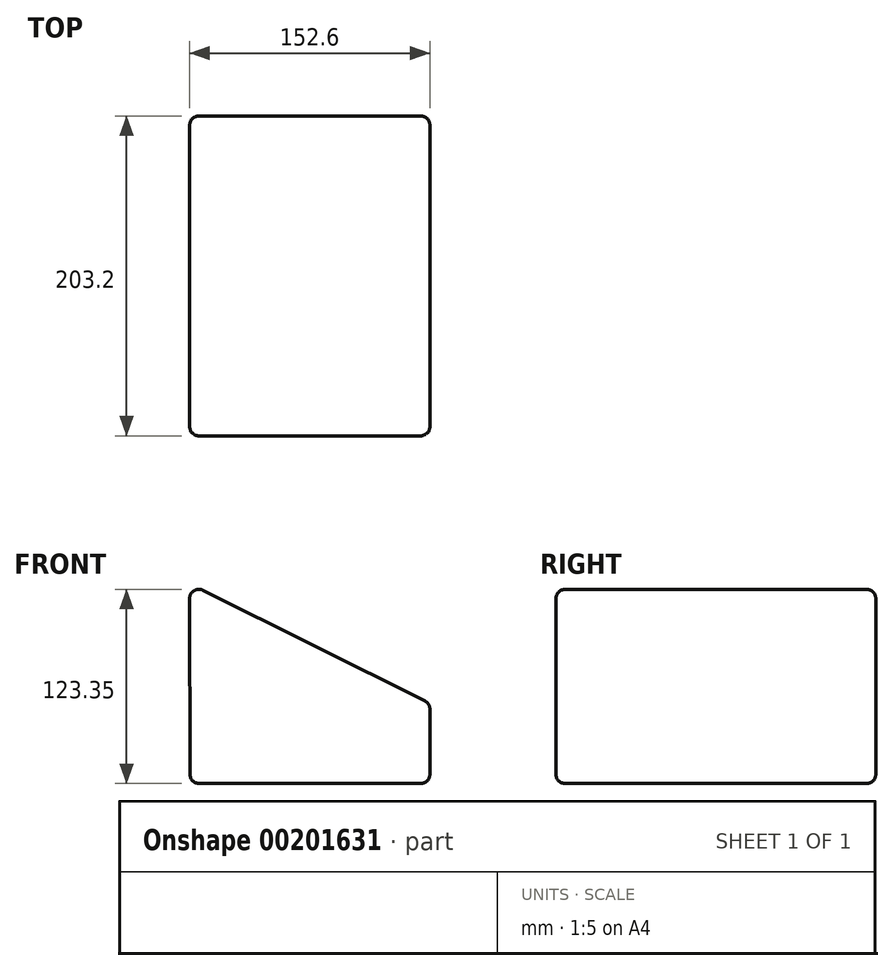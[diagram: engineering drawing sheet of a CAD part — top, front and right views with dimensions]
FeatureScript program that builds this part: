
annotation { "Feature Type Name" : "Feature", "Feature Type Description" : "" }
export const myFeature = defineFeature(function(context is Context, id is Id, definition is map)
    precondition{}
    {
        {
            var Q0;
            Q0=qCreatedBy(makeId("Front.planeOp"),FACE);
            var sketch = newSketch(context, id + "F0", { "sketchPlane" : qUnion([Q0])});
            skLineSegment(sketch, "E0", {"start": v(76.24, 0) * mm, "end": v(76.24, 50.8) * mm});
            skLineSegment(sketch, "E1", {"start": v(76.24, 50.8) * mm, "end": v(-76.38, 127) * mm});
            skLineSegment(sketch, "E2", {"start": v(-76.16, 0) * mm, "end": v(76.24, 0) * mm});
            skLineSegment(sketch, "E3", {"start": v(-76.38, 127) * mm, "end": v(-76.16, 0) * mm});
            skSolve(sketch);
        }
        {
            var Q0;
            Q0 = qSketchRegion(id + "F0", true);
            extrude(context, id + "F1", {"entities" : qUnion([Q0]), "endBound" : BoundingType.SYMMETRIC, "depth" : 203.2 * mm});
        }
        {
            var Q0;
            Q0=makeQuery(id+"F1.opExtrude","SWEPT_FACE",FACE,{"disambiguationData":[OSD([sQuery(id+"F0.wireOp",EDGE,"E1")])]});
            var Q1;
            Q1=makeQuery(id+"F1.opExtrude","SWEPT_FACE",FACE,{"disambiguationData":[OSD([sQuery(id+"F0.wireOp",EDGE,"E0")])]});
            var Q2;
            Q2=makeQuery(id+"F1.opExtrude","SWEPT_FACE",FACE,{"disambiguationData":[OSD([sQuery(id+"F0.wireOp",EDGE,"E2")])]});
            var Q3;
            Q3=makeQuery(id+"F1.opExtrude","SWEPT_FACE",FACE,{"disambiguationData":[OSD([sQuery(id+"F0.wireOp",EDGE,"E3")])]});
            fillet(context, id + "F2", {"entities" : qUnion([Q0, Q1, Q2, Q3]), "radius" : 5.9 * mm, "tangentPropagation" : true, "allowEdgeOverflow" : false});
        }
    });
